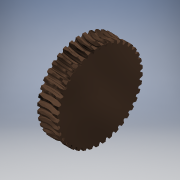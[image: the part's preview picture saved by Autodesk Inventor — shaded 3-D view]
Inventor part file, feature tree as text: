
AUTODESK INVENTOR PART (.ipt)
format: ipt  version: 2019.4 (Build 234330000, 330)  size: 3,965,952 bytes
history: native  units: mm
features: sketch x3, pattern_circular x3, other x2, helix x2, extrude x1, revolve x1, plane x1, projected_geometry x1
ambient origin geometry x8: Origin, YZ Plane, XZ Plane, XY Plane, X Axis, Y Axis, Z Axis, Center Point
bodies: Solid1 (feature_tree)
feature tree (14):
  extrude  "Extrusion1"  Depth=15.0mm TaperAngle=0.0deg
  other  "Work Axis1"
  revolve  "Revolution1"  [1 undecoded]
  sketch  "Sketch4"  dims[d9=2.574969mm d10=11.0mm d11=27.825mm d12=30.0mm d13=4.712389mm d14=10.0mm d15=25.0mm d16=0.0mm d17=90.0deg d18=90.0deg d19=0.0mm d20=0.0mm d30=4.712389mm d31=10.0mm d32=25.0mm d33=0.0mm d34=90.0deg d35=90.0deg d36=0.0mm d37=0.0mm d38=400.0mm d39=360.0deg d44=0.5mm d50=10.0mm d51=360.0deg d53=400.0mm d54=360.0deg d61=6.992874mm d64=1.5mm]
  helix  "Coil1"  [1 undecoded]
  helix  "Coil3"  [1 undecoded]
  pattern_circular  "Circular Pattern3"  [2 undecoded]
  pattern_circular  "Circular Pattern4"  [2 undecoded]
  pattern_circular  "Circular Pattern1"  Count=3  [1 undecoded]
  sketch  "Sketch1"  dims[d0=63.9mm d1=15.0mm d2=0.0mm]
  plane  "Work Plane2"
  other  "Work Point2"
  sketch  "Sketch3"  dims[d4=42.2mm d5=31.2mm d6=90.0deg d7=31.2mm]
  projected_geometry  "Projected Loop1"
note: 8 required parameter values undecoded (feature->parameter linkage not recoverable at this tier; creation-order binding heuristic only, values carry confidence <= 0.55)